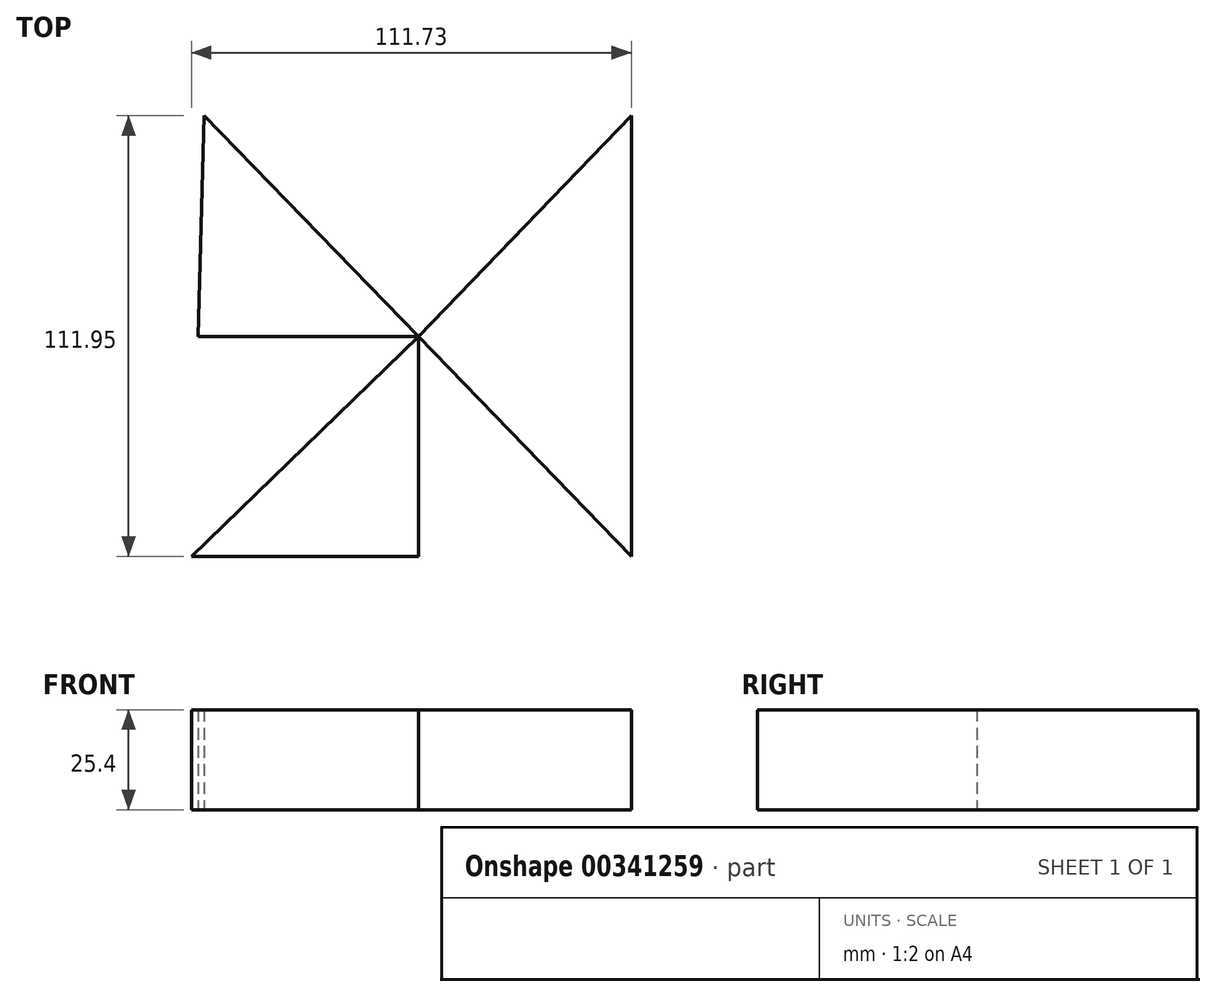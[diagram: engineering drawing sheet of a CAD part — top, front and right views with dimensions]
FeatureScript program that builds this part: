
annotation { "Feature Type Name" : "Feature", "Feature Type Description" : "" }
export const myFeature = defineFeature(function(context is Context, id is Id, definition is map)
    precondition{}
    {
        {
            var Q0;
            Q0=qCreatedBy(makeId("Top.planeOp"),FACE);
            var sketch = newSketch(context, id + "F0", { "sketchPlane" : qUnion([Q0])});
            skCircle(sketch, "E0", {"center": v(0, 0) * mm, "radius": 25.47 * mm});
            skLineSegment(sketch, "E1", {"start": v(0, 0) * mm, "end": v(54.1, 0) * mm});
            skLineSegment(sketch, "E2", {"start": v(0, 0) * mm, "end": v(54.1, -55.83) * mm});
            skLineSegment(sketch, "E3", {"start": v(54.1, -55.83) * mm, "end": v(54.1, 0) * mm});
            skLineSegment(sketch, "E4", {"start": v(54.1, 0) * mm, "end": v(54.1, 56.12) * mm});
            skLineSegment(sketch, "E5", {"start": v(54.1, 56.12) * mm, "end": v(0, 0) * mm});
            skLineSegment(sketch, "E6", {"start": v(0, 0) * mm, "end": v(0, 56.12) * mm});
            skLineSegment(sketch, "E7", {"start": v(0, 56.12) * mm, "end": v(54.1, 56.12) * mm});
            skLineSegment(sketch, "E8", {"start": v(0, 0) * mm, "end": v(0, -55.83) * mm});
            skLineSegment(sketch, "E9", {"start": v(0, -55.83) * mm, "end": v(54.1, -55.83) * mm});
            skLineSegment(sketch, "E10", {"start": v(0, 0) * mm, "end": v(-57.62, -55.83) * mm});
            skLineSegment(sketch, "E11", {"start": v(-57.62, -55.83) * mm, "end": v(0, -55.83) * mm});
            skLineSegment(sketch, "E12", {"start": v(0, 0) * mm, "end": v(-54.39, 56.12) * mm});
            skLineSegment(sketch, "E13", {"start": v(-54.39, 56.12) * mm, "end": v(0, 56.12) * mm});
            skLineSegment(sketch, "E14", {"start": v(-54.39, 56.12) * mm, "end": v(-57.62, -55.83) * mm});
            skLineSegment(sketch, "E15", {"start": v(-56, 0) * mm, "end": v(0, 0) * mm});
            skSolve(sketch);
        }
        {
            var Q0;
            {var subQ0=sQuery(id+"F0.wireOp",EDGE,"E12");var subQ1=sQuery(id+"F0.wireOp",EDGE,"E0");var subQ2=makeQuery(id+"F0.imprint","INTERSECT",VERTEX,{"derivedFrom":[subQ1,subQ0]});Q0=makeQuery(id+"F0.imprint","IMPRINT",FACE,{"disambiguationData":[TD([[makeQuery(id+"F0.imprint","IMPRINT",EDGE,{"disambiguationData":[TD([[subQ2,-1.0]])],"derivedFrom":subQ1}),-1.0]])]});}
            var Q1;
            {var subQ0=sQuery(id+"F0.wireOp",EDGE,"E12");var subQ1=sQuery(id+"F0.wireOp",EDGE,"E0");var subQ2=makeQuery(id+"F0.imprint","INTERSECT",VERTEX,{"derivedFrom":[subQ1,subQ0]});Q1=makeQuery(id+"F0.imprint","IMPRINT",FACE,{"disambiguationData":[TD([[makeQuery(id+"F0.imprint","IMPRINT",EDGE,{"disambiguationData":[TD([[subQ2,-1.0]])],"derivedFrom":subQ1}),1.0]])]});}
            var Q2;
            {var subQ0=sQuery(id+"F0.wireOp",EDGE,"E1");var subQ1=sQuery(id+"F0.wireOp",EDGE,"E0");var subQ2=makeQuery(id+"F0.imprint","INTERSECT",VERTEX,{"derivedFrom":[subQ1,subQ0]});Q2=makeQuery(id+"F0.imprint","IMPRINT",FACE,{"disambiguationData":[TD([[makeQuery(id+"F0.imprint","IMPRINT",EDGE,{"disambiguationData":[TD([[subQ2,1.0]])],"derivedFrom":subQ1}),1.0]])]});}
            var Q3;
            {var subQ5=sQuery(id+"F0.wireOp",EDGE,"E3");Q3=makeQuery(id+"F0.imprint","IMPRINT",FACE,{"disambiguationData":[TD([[makeQuery(id+"F0.imprint","IMPRINT",EDGE,{"derivedFrom":subQ5}),1.0]])]});}
            var Q4;
            {var subQ0=sQuery(id+"F0.wireOp",EDGE,"E10");var subQ1=sQuery(id+"F0.wireOp",EDGE,"E0");var subQ2=makeQuery(id+"F0.imprint","INTERSECT",VERTEX,{"derivedFrom":[subQ1,subQ0]});Q4=makeQuery(id+"F0.imprint","IMPRINT",FACE,{"disambiguationData":[TD([[makeQuery(id+"F0.imprint","IMPRINT",EDGE,{"disambiguationData":[TD([[subQ2,-1.0]])],"derivedFrom":subQ1}),1.0]])]});}
            var Q5;
            {var subQ5=sQuery(id+"F0.wireOp",EDGE,"E11");Q5=makeQuery(id+"F0.imprint","IMPRINT",FACE,{"disambiguationData":[TD([[makeQuery(id+"F0.imprint","IMPRINT",EDGE,{"derivedFrom":subQ5}),1.0]])]});}
            var Q6;
            {var subQ0=sQuery(id+"F0.wireOp",EDGE,"E5");var subQ1=sQuery(id+"F0.wireOp",EDGE,"E0");var subQ2=makeQuery(id+"F0.imprint","INTERSECT",VERTEX,{"derivedFrom":[subQ1,subQ0]});Q6=makeQuery(id+"F0.imprint","IMPRINT",FACE,{"disambiguationData":[TD([[makeQuery(id+"F0.imprint","IMPRINT",EDGE,{"disambiguationData":[TD([[subQ2,1.0]])],"derivedFrom":subQ1}),1.0]])]});}
            var Q7;
            {var subQ5=sQuery(id+"F0.wireOp",EDGE,"E4");Q7=makeQuery(id+"F0.imprint","IMPRINT",FACE,{"disambiguationData":[TD([[makeQuery(id+"F0.imprint","IMPRINT",EDGE,{"derivedFrom":subQ5}),1.0]])]});}
            extrude(context, id + "F1", {"entities" : qUnion([Q0, Q1, Q2, Q3, Q4, Q5, Q6, Q7]), "depth" : 25.4 * mm});
        }
    });
